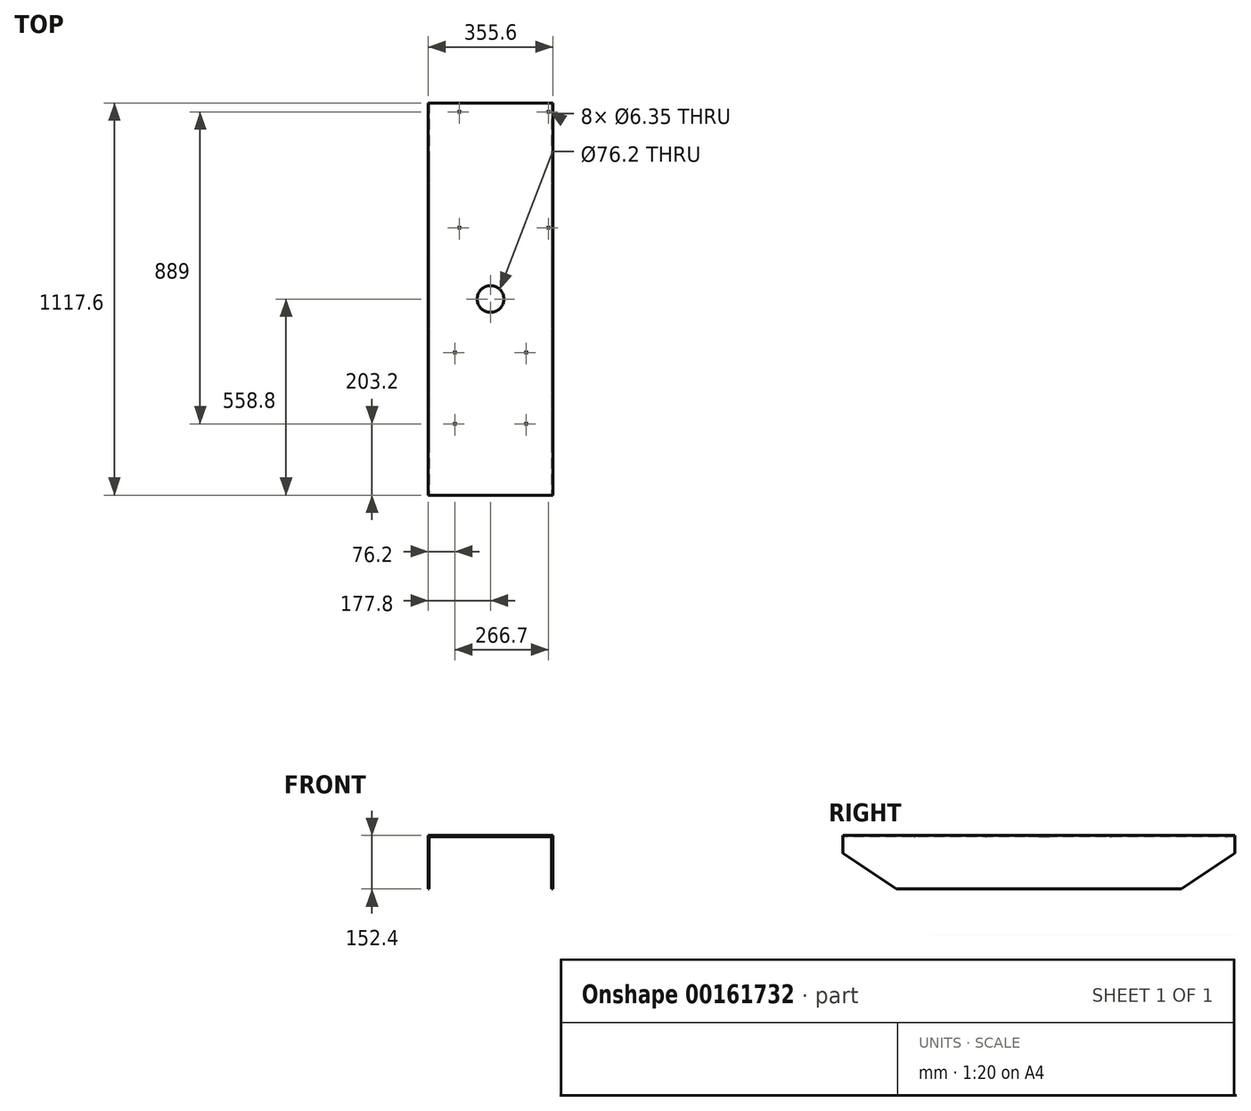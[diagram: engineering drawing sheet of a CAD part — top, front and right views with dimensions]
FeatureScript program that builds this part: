
annotation { "Feature Type Name" : "Feature", "Feature Type Description" : "" }
export const myFeature = defineFeature(function(context is Context, id is Id, definition is map)
    precondition{}
    {
        {
            var Q0;
            Q0=qCreatedBy(makeId("Right.planeOp"),FACE);
            var sketch = newSketch(context, id + "F0", { "sketchPlane" : qUnion([Q0])});
            skLineSegment(sketch, "E0", {"start": v(-558.8, 0) * mm, "end": v(558.8, 0) * mm});
            skLineSegment(sketch, "E1", {"start": v(-558.8, 0) * mm, "end": v(-558.8, -152.4) * mm});
            skLineSegment(sketch, "E2", {"start": v(-558.8, -152.4) * mm, "end": v(558.8, -152.4) * mm});
            skLineSegment(sketch, "E3", {"start": v(558.8, 0) * mm, "end": v(558.8, -152.4) * mm});
            skSolve(sketch);
        }
        {
            var Q0;
            Q0 = qSketchRegion(id + "F0", true);
            extrude(context, id + "F1", {"entities" : qUnion([Q0]), "oppositeDirection" : true, "depth" : 355.6 * mm});
        }
        {
            var Q0;
            Q0=makeQuery(id+"F1.opExtrude","SWEPT_FACE",FACE,{"disambiguationData":[OSD([sQuery(id+"F0.wireOp",EDGE,"E1")])]});
            var sketch = newSketch(context, id + "F2", { "sketchPlane" : qUnion([Q0])});
            skLineSegment(sketch, "E4", {"start": v(-355.6, -152.4) * mm, "end": v(-352.43, -152.4) * mm});
            skLineSegment(sketch, "E5", {"start": v(-352.43, -152.4) * mm, "end": v(-352.43, -3.17) * mm});
            skLineSegment(sketch, "E6", {"start": v(-352.43, -3.18) * mm, "end": v(-3.18, -3.18) * mm});
            skLineSegment(sketch, "E7", {"start": v(-3.18, -3.17) * mm, "end": v(-3.18, -152.4) * mm});
            skLineSegment(sketch, "E8", {"start": v(-3.18, -152.4) * mm, "end": v(0, -152.4) * mm});
            skLineSegment(sketch, "E9", {"start": v(0, -152.4) * mm, "end": v(0, 0) * mm});
            skLineSegment(sketch, "E10", {"start": v(0, 0) * mm, "end": v(-355.6, 0) * mm});
            skLineSegment(sketch, "E11", {"start": v(-355.6, 0) * mm, "end": v(-355.6, -152.4) * mm});
            skSolve(sketch);
        }
        {
            var Q0;
            {var subQ0=sQuery(id+"F2.wireOp",EDGE,"E5");Q0=makeQuery(id+"F2.imprint","IMPRINT",FACE,{"disambiguationData":[TD([[makeQuery(id+"F2.imprint","IMPRINT",EDGE,{"derivedFrom":subQ0}),-1.0]])]});}
            extrude(context, id + "F3", {"entities" : qUnion([Q0]), "operationType" : NewBodyOperationType.REMOVE, "endBound" : BoundingType.THROUGH_ALL, "oppositeDirection" : true, "depth" : 25.4 * mm});
        }
        {
            var Q0;
            Q0=makeQuery(id+"F1.opExtrude","CAP_FACE",FACE,{"disambiguationData":[OSD([sQuery(id+"F0.wireOp",EDGE,"E0"),sQuery(id+"F0.wireOp",EDGE,"E1"),sQuery(id+"F0.wireOp",EDGE,"E2"),sQuery(id+"F0.wireOp",EDGE,"E3")])],"isStart":true});
            var sketch = newSketch(context, id + "F4", { "sketchPlane" : qUnion([Q0])});
            skLineSegment(sketch, "E12", {"start": v(-558.8, 0) * mm, "end": v(-558.8, -50.8) * mm});
            skLineSegment(sketch, "E13", {"start": v(-558.8, -50.8) * mm, "end": v(-406.4, -152.4) * mm});
            skLineSegment(sketch, "E14", {"start": v(-406.4, -152.4) * mm, "end": v(406.4, -152.4) * mm});
            skLineSegment(sketch, "E15", {"start": v(406.4, -152.4) * mm, "end": v(558.8, -50.8) * mm});
            skLineSegment(sketch, "E16", {"start": v(558.8, -50.8) * mm, "end": v(558.8, 0) * mm});
            skLineSegment(sketch, "E17", {"start": v(558.8, 0) * mm, "end": v(-558.8, 0) * mm});
            skSolve(sketch);
        }
        {
            var Q0;
            {var subQ0=sQuery(id+"F4.wireOp",EDGE,"E13");Q0=makeQuery(id+"F4.imprint","IMPRINT",FACE,{"disambiguationData":[TD([[makeQuery(id+"F4.imprint","IMPRINT",EDGE,{"derivedFrom":subQ0}),-1.0]])]});}
            var Q1;
            {var subQ0=sQuery(id+"F4.wireOp",EDGE,"E15");Q1=makeQuery(id+"F4.imprint","IMPRINT",FACE,{"disambiguationData":[TD([[makeQuery(id+"F4.imprint","IMPRINT",EDGE,{"derivedFrom":subQ0}),-1.0]])]});}
            extrude(context, id + "F5", {"entities" : qUnion([Q0, Q1]), "operationType" : NewBodyOperationType.REMOVE, "endBound" : BoundingType.THROUGH_ALL, "oppositeDirection" : true, "depth" : 25.4 * mm});
        }
        {
            var Q0;
            Q0=makeQuery(id+"F1.opExtrude","SWEPT_FACE",FACE,{"disambiguationData":[OSD([sQuery(id+"F0.wireOp",EDGE,"E0")])]});
            var sketch = newSketch(context, id + "F6", { "sketchPlane" : qUnion([Q0])});
            skCircle(sketch, "E18", {"center": v(-177.8, 0) * mm, "radius": 38.1 * mm});
            skCircle(sketch, "E19", {"center": v(-12.7, 203.2) * mm, "radius": 3.18 * mm});
            skCircle(sketch, "E20", {"center": v(-266.7, 203.2) * mm, "radius": 3.18 * mm});
            skCircle(sketch, "E21", {"center": v(-266.7, 533.4) * mm, "radius": 3.18 * mm});
            skCircle(sketch, "E22", {"center": v(-12.7, 533.4) * mm, "radius": 3.18 * mm});
            skCircle(sketch, "E23", {"center": v(-76.2, -355.6) * mm, "radius": 3.18 * mm});
            skCircle(sketch, "E24", {"center": v(-76.2, -152.4) * mm, "radius": 3.18 * mm});
            skCircle(sketch, "E25", {"center": v(-279.4, -152.4) * mm, "radius": 3.18 * mm});
            skCircle(sketch, "E26", {"center": v(-279.4, -355.6) * mm, "radius": 3.18 * mm});
            skSolve(sketch);
        }
        {
            var Q0;
            Q0 = qSketchRegion(id + "F6", true);
            extrude(context, id + "F7", {"entities" : qUnion([Q0]), "operationType" : NewBodyOperationType.REMOVE, "endBound" : BoundingType.THROUGH_ALL, "oppositeDirection" : true, "depth" : 25.4 * mm});
        }
    });
